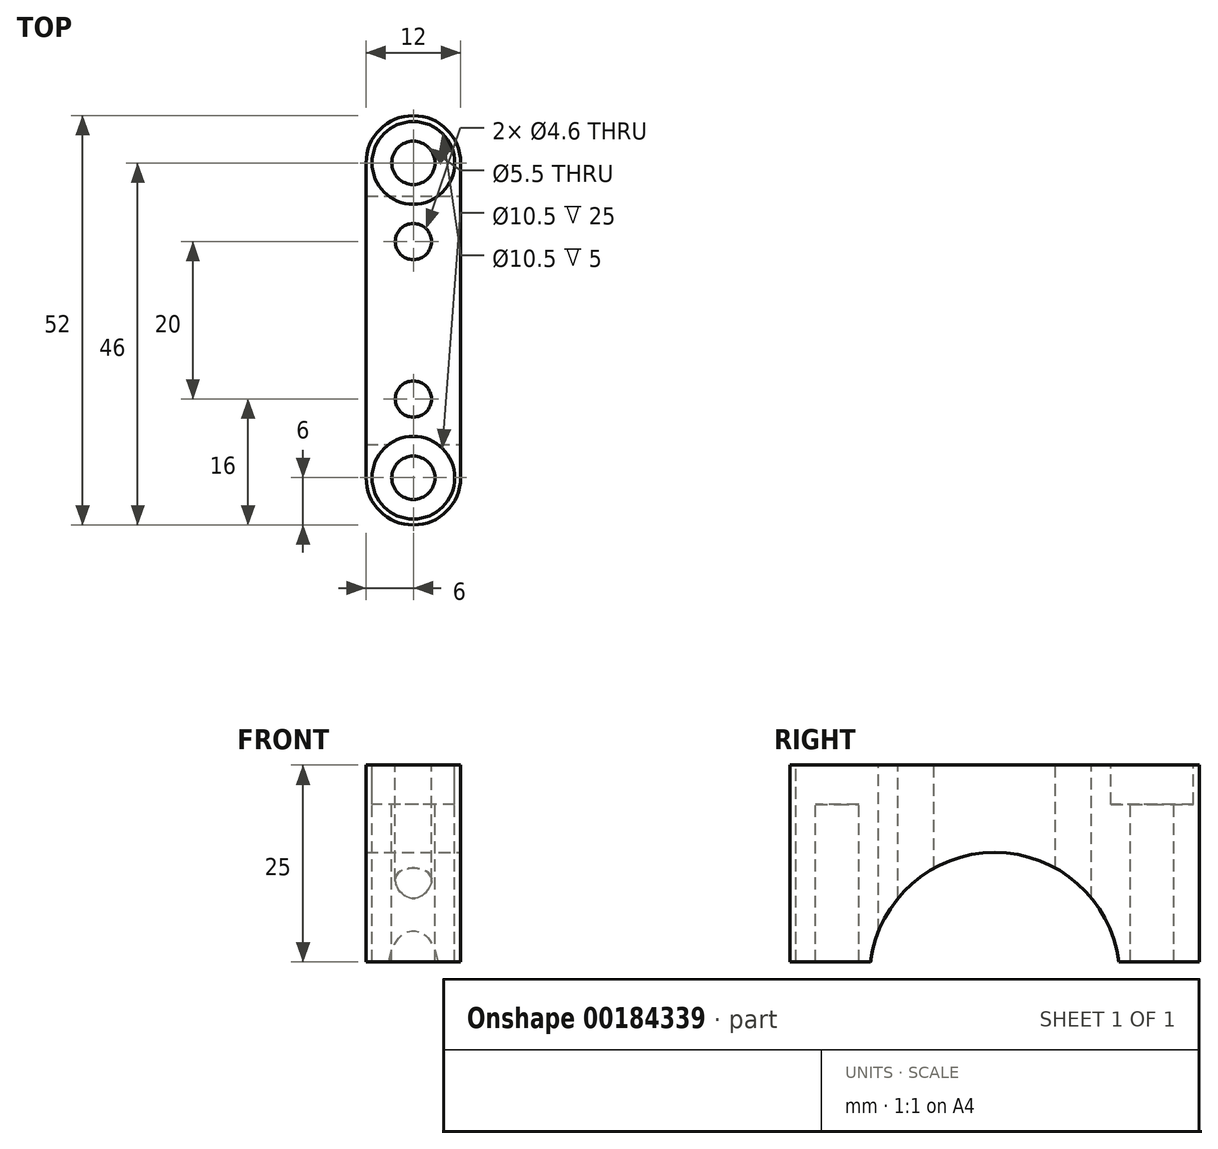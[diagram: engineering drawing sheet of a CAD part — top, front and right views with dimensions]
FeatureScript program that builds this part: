
annotation { "Feature Type Name" : "Feature", "Feature Type Description" : "" }
export const myFeature = defineFeature(function(context is Context, id is Id, definition is map)
    precondition{}
    {
        {
            var Q0;
            Q0=qCreatedBy(makeId("Top.planeOp"),FACE);
            var sketch = newSketch(context, id + "F0", { "sketchPlane" : qUnion([Q0])});
            skLineSegment(sketch, "E0.bottom", {"start": v(6, 26) * mm, "end": v(-6, 26) * mm});
            skLineSegment(sketch, "E0.top", {"start": v(6, -26) * mm, "end": v(-6, -26) * mm});
            skLineSegment(sketch, "E0.left", {"start": v(6, 26) * mm, "end": v(6, -26) * mm});
            skLineSegment(sketch, "E0.right", {"start": v(-6, 26) * mm, "end": v(-6, -26) * mm});
            skPoint(sketch, "E0.middle", {"position": v(0, 0) * mm});
            skCircle(sketch, "E1", {"center": v(0, 20) * mm, "radius": 2.75 * mm});
            skCircle(sketch, "E2.MirrorC", {"center": v(0, -20) * mm, "radius": 2.75 * mm});
            skCircle(sketch, "E3.0", {"center": v(0, 20) * mm, "radius": 5.25 * mm});
            skCircle(sketch, "E4.0", {"center": v(0, -20) * mm, "radius": 5.25 * mm});
            skCircle(sketch, "E5", {"center": v(0, 10) * mm, "radius": 2.3 * mm});
            skCircle(sketch, "E6.MirrorC", {"center": v(0, -10) * mm, "radius": 2.3 * mm});
            skSolve(sketch);
        }
        {
            var Q0;
            Q0=makeQuery(id+"F0.imprint","IMPRINT",FACE,{"disambiguationData":[TD([[makeQuery(id+"F0.imprint","IMPRINT",EDGE,{"derivedFrom":sQuery(id+"F0.wireOp",EDGE,"E0.bottom")}),1.0]])]});
            var Q1;
            Q1=makeQuery(id+"F0.imprint","IMPRINT",FACE,{"disambiguationData":[TD([[makeQuery(id+"F0.imprint","IMPRINT",EDGE,{"derivedFrom":sQuery(id+"F0.wireOp",EDGE,"E1")}),-1.0]])]});
            var Q2;
            Q2=makeQuery(id+"F0.imprint","IMPRINT",FACE,{"disambiguationData":[TD([[makeQuery(id+"F0.imprint","IMPRINT",EDGE,{"derivedFrom":sQuery(id+"F0.wireOp",EDGE,"E2.MirrorC")}),1.0]])]});
            extrude(context, id + "F1", {"entities" : qUnion([Q0, Q1, Q2]), "oppositeDirection" : true, "depth" : 25 * mm, "offsetDistance" : 25 * mm});
        }
        {
            var Q0;
            Q0=makeQuery(id+"F0.imprint","IMPRINT",FACE,{"disambiguationData":[TD([[makeQuery(id+"F0.imprint","IMPRINT",EDGE,{"derivedFrom":sQuery(id+"F0.wireOp",EDGE,"E1")}),-1.0]])]});
            var Q1;
            Q1=makeQuery(id+"F0.imprint","IMPRINT",FACE,{"disambiguationData":[TD([[makeQuery(id+"F0.imprint","IMPRINT",EDGE,{"derivedFrom":sQuery(id+"F0.wireOp",EDGE,"E2.MirrorC")}),1.0]])]});
            extrude(context, id + "F2", {"entities" : qUnion([Q0, Q1]), "operationType" : NewBodyOperationType.REMOVE, "oppositeDirection" : true, "depth" : 5 * mm, "offsetDistance" : 25 * mm});
        }
        {
            var Q0;
            Q0=makeQuery(id+"F1.opExtrude","SWEPT_FACE",FACE,{"disambiguationData":[OSD([sQuery(id+"F0.wireOp",EDGE,"E0.left")])]});
            var sketch = newSketch(context, id + "F3", { "sketchPlane" : qUnion([Q0])});
            skCircle(sketch, "E7", {"center": v(0, -27) * mm, "radius": 15.9 * mm});
            skSolve(sketch);
        }
        {
            var Q0;
            {var subQ0=sQuery(id+"F3.wireOp",EDGE,"E7");var subQ1=makeQuery(id+"F1.opExtrude","CAP_EDGE",EDGE,{"disambiguationData":[OSD([sQuery(id+"F0.wireOp",EDGE,"E0.left")])],"isStart":false});var subQ2=makeQuery(id+"F3.imprint","INTERSECT",VERTEX,{"disambiguationData":[OD(0.0)],"derivedFrom":[subQ1,subQ0]});Q0=makeQuery(id+"F3.imprint","IMPRINT",FACE,{"disambiguationData":[TD([[makeQuery(id+"F3.imprint","IMPRINT",EDGE,{"disambiguationData":[TD([[subQ2,-1.0]])],"derivedFrom":subQ0}),1.0]])]});}
            extrude(context, id + "F4", {"entities" : qUnion([Q0]), "operationType" : NewBodyOperationType.REMOVE, "endBound" : BoundingType.THROUGH_ALL, "oppositeDirection" : true, "depth" : 25 * mm, "offsetDistance" : 25 * mm});
        }
        {
            var Q0;
            Q0=makeQuery(id+"F1.opExtrude","SWEPT_EDGE",EDGE,{"disambiguationData":[OSD([sQuery(id+"F0.wireOp",EDGE,"E0.bottom"),sQuery(id+"F0.wireOp",EDGE,"E0.right")])]});
            var Q1;
            Q1=makeQuery(id+"F1.opExtrude","SWEPT_EDGE",EDGE,{"disambiguationData":[OSD([sQuery(id+"F0.wireOp",EDGE,"E0.bottom"),sQuery(id+"F0.wireOp",EDGE,"E0.left")])]});
            var Q2;
            Q2=makeQuery(id+"F1.opExtrude","SWEPT_EDGE",EDGE,{"disambiguationData":[OSD([sQuery(id+"F0.wireOp",EDGE,"E0.top"),sQuery(id+"F0.wireOp",EDGE,"E0.left")])]});
            var Q3;
            Q3=makeQuery(id+"F1.opExtrude","SWEPT_EDGE",EDGE,{"disambiguationData":[OSD([sQuery(id+"F0.wireOp",EDGE,"E0.top"),sQuery(id+"F0.wireOp",EDGE,"E0.right")])]});
            fillet(context, id + "F5", {"entities" : qUnion([Q0, Q1, Q2, Q3]), "tangentPropagation" : true, "radius" : 6 * mm, "defaultsChanged" : true, "vertexSettings" : [], "allowEdgeOverflow" : false});
        }
    });
